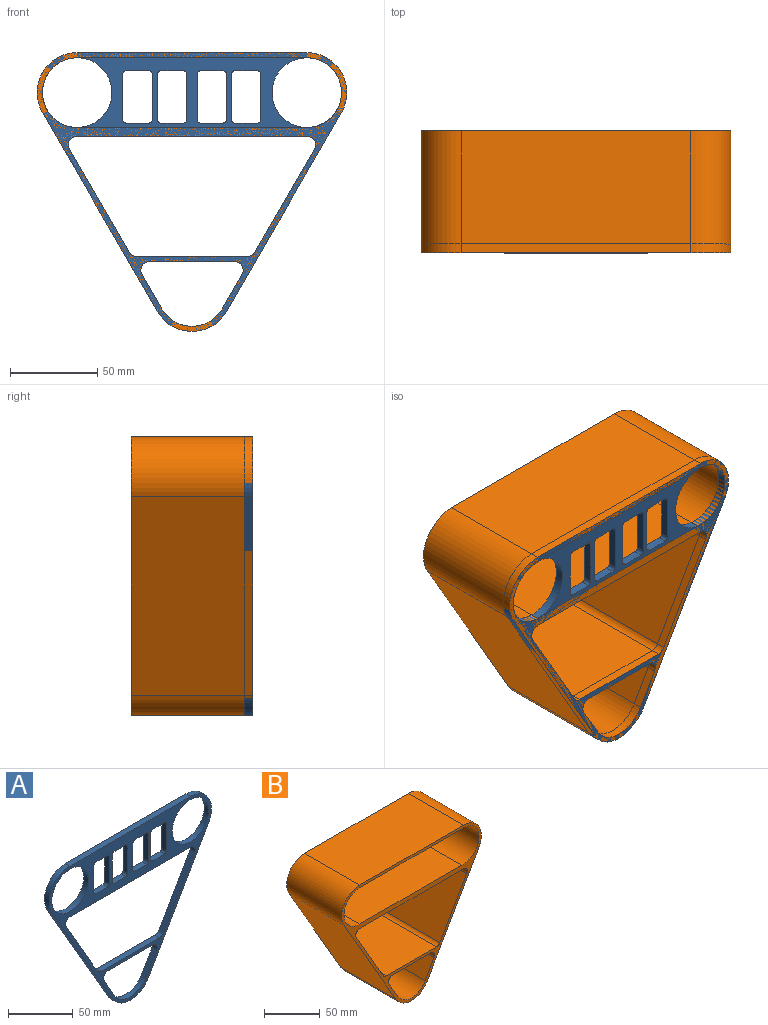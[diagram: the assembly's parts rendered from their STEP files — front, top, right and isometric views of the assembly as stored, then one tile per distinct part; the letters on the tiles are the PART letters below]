
ASSEMBLY  parts=2 mates=1
PART A: 56 faces, bbox 177.9x5x160.3 mm
  f0: plane 114.27x65.97mm, normal (-0.87,0,-0.5), area 659.7mm2, adj f1,f53,f54,f55
  f1: cylinder r=23mm len=39.84mm, axis (0,1,0), area 240.9mm2, adj f0,f2,f54,f55
  f2: plane 114.27x65.97mm, normal (0.87,0,-0.5), area 659.7mm2, adj f1,f3,f54,f55
  f3: cylinder r=23mm len=34.5mm, axis (0,1,0), area 240.9mm2, adj f2,f4,f54,f55
  f4: plane 131.95x5mm, normal (0,0,1), area 659.7mm2, adj f3,f53,f54,f55
  f5: cylinder r=5mm len=7.5mm, axis (0,1,0), area 52.4mm2, adj f6,f46,f54,f55
  f6: plane 48.78x5mm, normal (0,0,-1), area 243.9mm2, adj f5,f7,f54,f55
  f7: cylinder r=5mm len=7.5mm, axis (0,1,0), area 52.4mm2, adj f6,f8,f54,f55
  f8: plane 19.74x11.4mm, normal (-0.87,0,0.5), area 114mm2, adj f7,f9,f54,f55
  f9: cylinder r=20mm len=34.64mm, axis (0,1,0), area 209.4mm2, adj f8,f46,f54,f55
  f10: plane 13x5mm, normal (0,0,1), area 65mm2, adj f11,f47,f54,f55
  f11: cylinder r=2mm len=5mm, axis (0,1,0), area 15.7mm2, adj f10,f12,f54,f55
  f12: plane 26x5mm, normal (1,0,0), area 130mm2, adj f11,f13,f54,f55
  f13: cylinder r=2mm len=5mm, axis (0,1,0), area 15.7mm2, adj f12,f14,f54,f55
  f14: plane 13x5mm, normal (0,0,-1), area 65mm2, adj f13,f15,f54,f55
  f15: cylinder r=2mm len=5mm, axis (0,1,0), area 15.7mm2, adj f14,f16,f54,f55
  f16: plane 26x5mm, normal (-1,0,0), area 130mm2, adj f15,f47,f54,f55
  f17: plane 13x5mm, normal (0,0,1), area 65mm2, adj f18,f48,f54,f55
  f18: cylinder r=2mm len=5mm, axis (0,1,0), area 15.7mm2, adj f17,f19,f54,f55
  f19: plane 26x5mm, normal (1,0,0), area 130mm2, adj f18,f20,f54,f55
  f20: cylinder r=2mm len=5mm, axis (0,1,0), area 15.7mm2, adj f19,f21,f54,f55
  f21: plane 13x5mm, normal (0,0,-1), area 65mm2, adj f20,f22,f54,f55
  f22: cylinder r=2mm len=5mm, axis (0,1,0), area 15.7mm2, adj f21,f23,f54,f55
  f23: plane 26x5mm, normal (-1,0,0), area 130mm2, adj f22,f48,f54,f55
  f24: plane 13x5mm, normal (0,0,1), area 65mm2, adj f25,f49,f54,f55
  f25: cylinder r=2mm len=5mm, axis (0,1,0), area 15.7mm2, adj f24,f26,f54,f55
  f26: plane 26x5mm, normal (1,0,0), area 130mm2, adj f25,f27,f54,f55
  f27: cylinder r=2mm len=5mm, axis (0,1,0), area 15.7mm2, adj f26,f28,f54,f55
  f28: plane 13x5mm, normal (0,0,-1), area 65mm2, adj f27,f29,f54,f55
  f29: cylinder r=2mm len=5mm, axis (0,1,0), area 15.7mm2, adj f28,f30,f54,f55
  f30: plane 26x5mm, normal (-1,0,0), area 130mm2, adj f29,f49,f54,f55
  f31: plane 13x5mm, normal (0,0,1), area 65mm2, adj f32,f50,f54,f55
  f32: cylinder r=2mm len=5mm, axis (0,1,0), area 15.7mm2, adj f31,f33,f54,f55
  f33: plane 26x5mm, normal (1,0,0), area 130mm2, adj f32,f34,f54,f55
  f34: cylinder r=2mm len=5mm, axis (0,1,0), area 15.7mm2, adj f33,f35,f54,f55
  f35: plane 13x5mm, normal (0,0,-1), area 65mm2, adj f34,f36,f54,f55
  f36: cylinder r=2mm len=5mm, axis (0,1,0), area 15.7mm2, adj f35,f37,f54,f55
  f37: plane 26x5mm, normal (-1,0,0), area 130mm2, adj f36,f50,f54,f55
  f38: plane 131.95x5mm, normal (0,0,-1), area 659.7mm2, adj f39,f51,f54,f55
  f39: cylinder r=5mm len=7.5mm, axis (0,1,0), area 52.4mm2, adj f38,f40,f54,f55
  f40: plane 59.03x34.08mm, normal (-0.87,0,0.5), area 340.8mm2, adj f39,f41,f54,f55
  f41: cylinder r=5mm len=5mm, axis (0,1,0), area 26.2mm2, adj f40,f42,f54,f55
  f42: plane 63.79x5mm, normal (0,0,1), area 318.9mm2, adj f41,f43,f54,f55
  f43: cylinder r=5mm len=5mm, axis (0,1,0), area 26.2mm2, adj f42,f44,f54,f55
  f44: plane 59.03x34.08mm, normal (0.87,0,0.5), area 340.8mm2, adj f43,f51,f54,f55
  f45: cylinder r=20mm len=40mm, axis (0,1,0), area 628.3mm2, adj f54,f55
  f46: plane 19.74x11.4mm, normal (0.87,0,0.5), area 114mm2, adj f5,f9,f54,f55
  f47: cylinder r=2mm len=5mm, axis (0,1,0), area 15.7mm2, adj f10,f16,f54,f55
  f48: cylinder r=2mm len=5mm, axis (0,1,0), area 15.7mm2, adj f17,f23,f54,f55
  f49: cylinder r=2mm len=5mm, axis (0,1,0), area 15.7mm2, adj f24,f30,f54,f55
  f50: cylinder r=2mm len=5mm, axis (0,1,0), area 15.7mm2, adj f31,f37,f54,f55
  f51: cylinder r=5mm len=7.5mm, axis (0,1,0), area 52.4mm2, adj f38,f44,f54,f55
  f52: cylinder r=20mm len=40mm, axis (0,1,0), area 628.3mm2, adj f54,f55
  f53: cylinder r=23mm len=34.5mm, axis (0,1,0), area 240.9mm2, adj f0,f4,f54,f55
  f54: plane 177.95x160.27mm, normal (0,-1,0), area 4666.3mm2, adj f0,f1,f2,f3,f4,f5,f6,f7
  f55: plane 177.95x160.27mm, normal (0,1,0), area 4666.3mm2, adj f0,f1,f2,f3,f4,f5,f6,f7
PART B: 26 faces, bbox 177.9x70x160.3 mm
  f0: plane 114.27x70mm, normal (-0.87,0,-0.5), area 9236.4mm2, adj f1,f23,f24,f25
  f1: cylinder r=23mm len=70mm, axis (0,1,0), area 3372mm2, adj f0,f2,f24,f25
  f2: plane 114.27x70mm, normal (0.87,0,-0.5), area 9236.4mm2, adj f1,f3,f24,f25
  f3: cylinder r=23mm len=70mm, axis (0,1,0), area 3372mm2, adj f2,f4,f24,f25
  f4: plane 131.95x70mm, normal (0,0,1), area 9236.4mm2, adj f3,f23,f24,f25
  f5: plane 129.64x70mm, normal (0,0,1), area 9075mm2, adj f6,f20,f24,f25
  f6: cylinder r=20mm len=70mm, axis (0,1,0), area 4398.2mm2, adj f5,f7,f24,f25
  f7: plane 131.95x70mm, normal (0,0,-1), area 9236.4mm2, adj f6,f20,f24,f25
  f8: cylinder r=5mm len=70mm, axis (0,1,0), area 366.5mm2, adj f9,f21,f24,f25
  f9: plane 70x59.03mm, normal (0.87,0,0.5), area 4771.1mm2, adj f8,f10,f24,f25
  f10: cylinder r=5mm len=70mm, axis (0,1,0), area 733mm2, adj f9,f11,f24,f25
  f11: plane 131.95x70mm, normal (0,0,-1), area 9236.4mm2, adj f10,f12,f24,f25
  f12: cylinder r=5mm len=70mm, axis (0,1,0), area 733mm2, adj f11,f13,f24,f25
  f13: plane 70x59.03mm, normal (-0.87,0,0.5), area 4771.1mm2, adj f12,f14,f24,f25
  f14: cylinder r=5mm len=70mm, axis (0,1,0), area 366.5mm2, adj f13,f21,f24,f25
  f15: cylinder r=5mm len=70mm, axis (0,1,0), area 733mm2, adj f16,f22,f24,f25
  f16: plane 70x48.78mm, normal (0,0,-1), area 3414.5mm2, adj f15,f17,f24,f25
  f17: cylinder r=5mm len=70mm, axis (0,1,0), area 733mm2, adj f16,f18,f24,f25
  f18: plane 70x19.74mm, normal (-0.87,0,0.5), area 1595.9mm2, adj f17,f19,f24,f25
  f19: cylinder r=20mm len=70mm, axis (0,1,0), area 2932.2mm2, adj f18,f22,f24,f25
  f20: cylinder r=20mm len=70mm, axis (0,1,0), area 4560mm2, adj f5,f7,f24,f25
  f21: plane 70x63.79mm, normal (0,0,1), area 4465.3mm2, adj f8,f14,f24,f25
  f22: plane 70x19.74mm, normal (0.87,0,0.5), area 1595.9mm2, adj f15,f19,f24,f25
  f23: cylinder r=23mm len=70mm, axis (0,1,0), area 3372mm2, adj f0,f4,f24,f25
  f24: plane 177.95x160.27mm, normal (0,-1,0), area 2680mm2, adj f0,f1,f2,f3,f4,f5,f6,f7
  f25: plane 177.95x160.27mm, normal (0,1,0), area 2680mm2, adj f0,f1,f2,f3,f4,f5,f6,f7
PLACE A t=(-1.11,-38.2,11.33)mm
PLACE B t=(-1.09,29.3,-18.44)mm
MATE fastened A.f54 <-> B.f24  axis (0,-1,0) through (-21.01,-40.7,-76.24)mm
